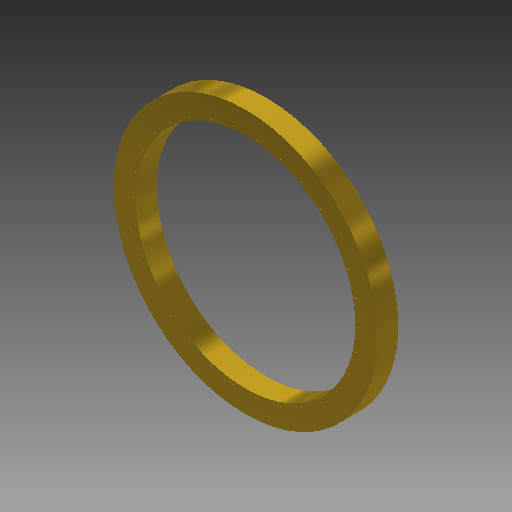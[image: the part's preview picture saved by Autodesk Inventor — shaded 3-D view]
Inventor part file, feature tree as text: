
AUTODESK INVENTOR PART (.ipt)
format: ipt  version: 2017 (Build 210142000, 142)  size: 196,096 bytes
history: native  units: in
note: dims shown in document units (in); Inventor stores cm internally (conversion verified against a paired STEP export)
features: other x3, sketch x2, projected_geometry x2, extrude x1, hole x1, pattern_circular x1
ambient origin geometry x8: Origin, YZ Plane, XZ Plane, XY Plane, X Axis, Y Axis, Z Axis, Center Point
bodies: Solid1 (feature_tree)
feature tree (10):
  other  "Electrode 5_6_7.ipt"
  extrude  "Extrusion1"  Depth=0.3937in TaperAngle=0.0deg
  hole  "Hole1"  [1 undecoded]
  pattern_circular  "Circular Pattern1"  [2 undecoded]
  other  "Solid1::Electrode 5_6_7.ipt"
  other  "TaggingFeature1"
  sketch  "Sketch1"  dims[d0=0.3937in d1=1.0in d2=0.0in]
  projected_geometry  "Projected Loop1"
  projected_geometry  "Projected Loop2"
  sketch  "Sketch2"  dims[d3=4.47in d4=0.163in d5=0.75in d6=0.375in d7=0.25in d8=0.5635in d9=0.3937in d10=0.8108in d11=1.1811in d12=360.0deg]
note: 3 required parameter values undecoded (feature->parameter linkage not recoverable at this tier; creation-order binding heuristic only, values carry confidence <= 0.55)
